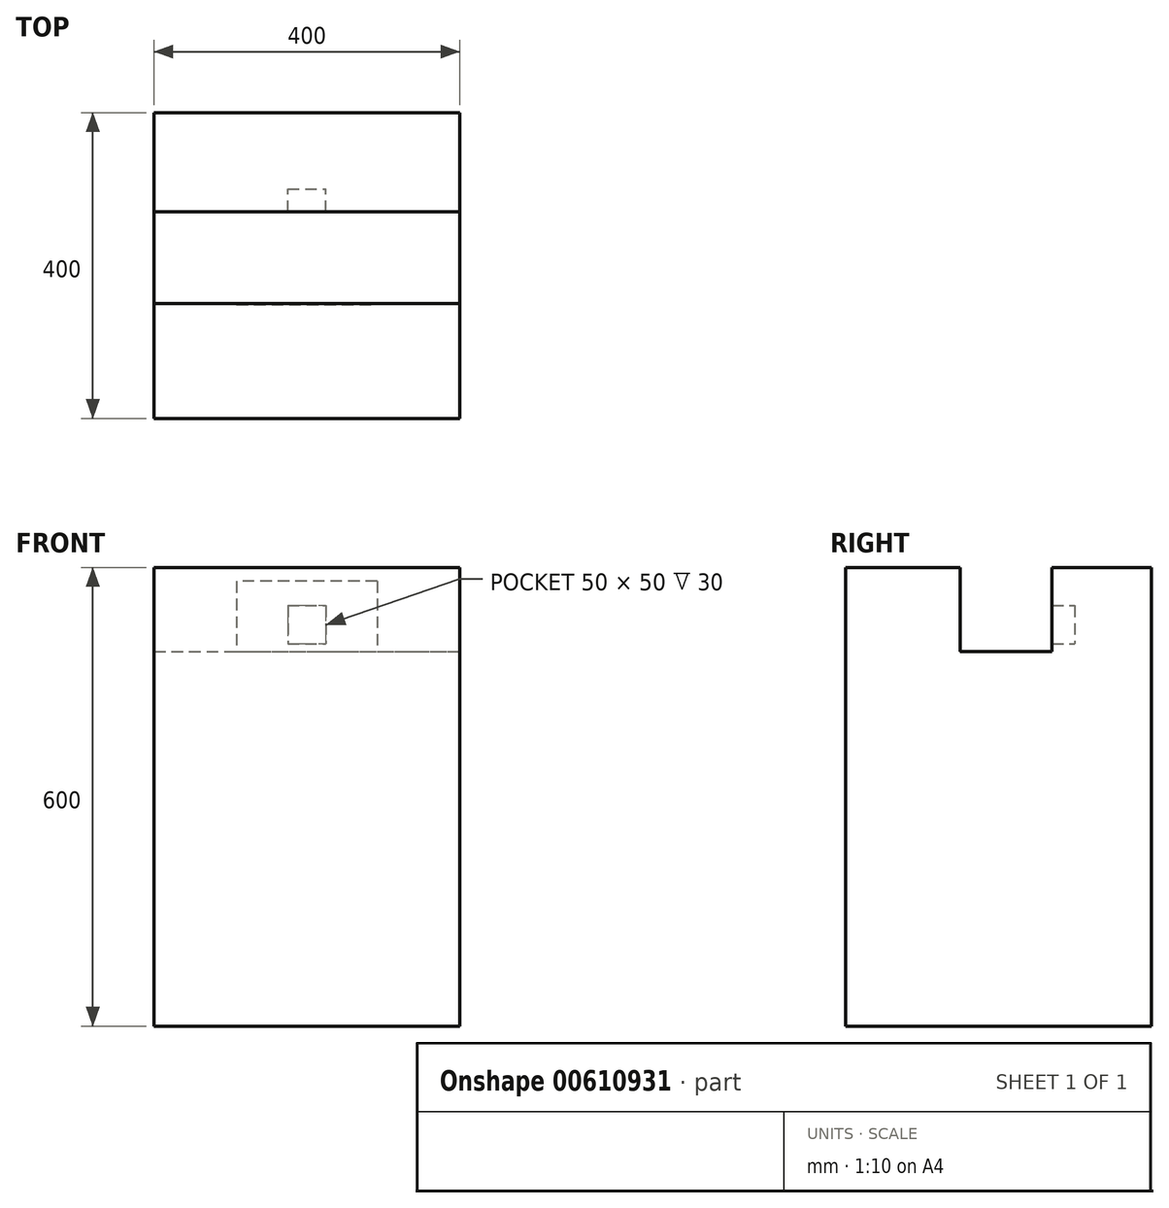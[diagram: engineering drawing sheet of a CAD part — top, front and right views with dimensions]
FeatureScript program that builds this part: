
annotation { "Feature Type Name" : "Feature", "Feature Type Description" : "" }
export const myFeature = defineFeature(function(context is Context, id is Id, definition is map)
    precondition{}
    {
        {
            var Q0;
            Q0=qCreatedBy(makeId("Right.planeOp"),FACE);
            var sketch = newSketch(context, id + "F0", { "sketchPlane" : qUnion([Q0])});
            skLineSegment(sketch, "E0.bottom", {"start": v(0, 0) * mm, "end": v(400, 0) * mm});
            skLineSegment(sketch, "E0.top", {"start": v(0, 600) * mm, "end": v(400, 600) * mm});
            skLineSegment(sketch, "E0.left", {"start": v(0, 0) * mm, "end": v(0, 600) * mm});
            skLineSegment(sketch, "E0.right", {"start": v(400, 0) * mm, "end": v(400, 600) * mm});
            skSolve(sketch);
        }
        {
            var Q0;
            Q0=makeQuery(id+"F0.imprint","IMPRINT",FACE,{"disambiguationData":[TD([[makeQuery(id+"F0.imprint","IMPRINT",EDGE,{"derivedFrom":sQuery(id+"F0.wireOp",EDGE,"E0.bottom")}),1.0]])]});
            extrude(context, id + "F1", {"entities" : qUnion([Q0]), "depth" : 200 * mm, "offsetDistance" : 25 * mm});
        }
        {
            var Q0;
            Q0=makeQuery(id+"F1.opExtrude","CAP_FACE",FACE,{"disambiguationData":[OSD([sQuery(id+"F0.wireOp",EDGE,"E0.bottom"),sQuery(id+"F0.wireOp",EDGE,"E0.top"),sQuery(id+"F0.wireOp",EDGE,"E0.left"),sQuery(id+"F0.wireOp",EDGE,"E0.right")])],"isStart":false});
            var sketch = newSketch(context, id + "F2", { "sketchPlane" : qUnion([Q0])});
            skLineSegment(sketch, "E1.bottom", {"start": v(270, 550) * mm, "end": v(300, 550) * mm});
            skLineSegment(sketch, "E1.top", {"start": v(270, 500) * mm, "end": v(300, 500) * mm});
            skLineSegment(sketch, "E1.left", {"start": v(270, 550) * mm, "end": v(270, 500) * mm});
            skLineSegment(sketch, "E1.right", {"start": v(300, 550) * mm, "end": v(300, 500) * mm});
            skSolve(sketch);
        }
        {
            var Q0;
            Q0=makeQuery(id+"F2.imprint","IMPRINT",FACE,{"disambiguationData":[TD([[makeQuery(id+"F2.imprint","IMPRINT",EDGE,{"derivedFrom":sQuery(id+"F2.wireOp",EDGE,"E1.bottom")}),-1.0]])]});
            extrude(context, id + "F3", {"entities" : qUnion([Q0]), "operationType" : NewBodyOperationType.REMOVE, "oppositeDirection" : true, "depth" : 25 * mm, "offsetDistance" : 25 * mm});
        }
        {
            var Q0;
            Q0=makeQuery(id+"F1.opExtrude","CAP_FACE",FACE,{"disambiguationData":[OSD([sQuery(id+"F0.wireOp",EDGE,"E0.bottom"),sQuery(id+"F0.wireOp",EDGE,"E0.top"),sQuery(id+"F0.wireOp",EDGE,"E0.left"),sQuery(id+"F0.wireOp",EDGE,"E0.right")])],"isStart":false});
            extrude(context, id + "F4", {"entities" : qUnion([Q0]), "operationType" : NewBodyOperationType.ADD, "depth" : 25 * mm, "offsetDistance" : 25 * mm});
        }
        {
            var Q0;
            Q0=makeQuery(id+"F4.opExtrude","CAP_FACE",FACE,{"disambiguationData":[OSD([sQuery(id+"F0.wireOp",EDGE,"E0.bottom"),sQuery(id+"F0.wireOp",EDGE,"E0.top"),sQuery(id+"F0.wireOp",EDGE,"E0.left"),sQuery(id+"F0.wireOp",EDGE,"E0.right")])],"isStart":false});
            var sketch = newSketch(context, id + "F5", { "sketchPlane" : qUnion([Q0])});
            skLineSegment(sketch, "E2.0", {"start": v(0, 600) * mm, "end": v(400, 600) * mm});
            skLineSegment(sketch, "E3.0", {"start": v(0, 0) * mm, "end": v(0, 600) * mm});
            skLineSegment(sketch, "E4.0", {"start": v(0, 0) * mm, "end": v(400, 0) * mm});
            skLineSegment(sketch, "E5.0", {"start": v(400, 0) * mm, "end": v(400, 600) * mm});
            skSolve(sketch);
        }
        {
            var Q0;
            Q0=makeQuery(id+"F5.imprint","IMPRINT",FACE,{"disambiguationData":[TD([[makeQuery(id+"F5.imprint","IMPRINT",EDGE,{"derivedFrom":sQuery(id+"F5.wireOp",EDGE,"E2.0")}),-1.0]])]});
            var Q1;
            Q1=makeQuery(id+"F5.imprint","IMPRINT",FACE,{"disambiguationData":[TD([[makeQuery(id+"F5.imprint","IMPRINT",EDGE,{"derivedFrom":makeQuery(id+"F4.opExtrude","CAP_EDGE",EDGE,{"disambiguationData":[OSD([sQuery(id+"F2.wireOp",EDGE,"E1.bottom")])],"isStart":false})}),-1.0]])]});
            extrude(context, id + "F6", {"entities" : qUnion([Q0, Q1]), "operationType" : NewBodyOperationType.ADD, "depth" : (200 - 25) * mm, "offsetDistance" : 25 * mm});
        }
        {
            var Q0;
            Q0=makeQuery(id+"F6.opExtrude","CAP_FACE",FACE,{"disambiguationData":[OSD([sQuery(id+"F5.wireOp",EDGE,"E2.0"),sQuery(id+"F5.wireOp",EDGE,"E3.0"),sQuery(id+"F5.wireOp",EDGE,"E4.0"),sQuery(id+"F5.wireOp",EDGE,"E5.0")])],"isStart":false});
            var sketch = newSketch(context, id + "F7", { "sketchPlane" : qUnion([Q0])});
            skLineSegment(sketch, "E6.bottom", {"start": v(270, 600) * mm, "end": v(150, 600) * mm});
            skLineSegment(sketch, "E6.top", {"start": v(270, 490) * mm, "end": v(150, 490) * mm});
            skLineSegment(sketch, "E6.left", {"start": v(270, 600) * mm, "end": v(270, 490) * mm});
            skLineSegment(sketch, "E6.right", {"start": v(150, 600) * mm, "end": v(150, 490) * mm});
            skLineSegment(sketch, "E7.0", {"start": v(270, 550) * mm, "end": v(270, 500) * mm});
            skSolve(sketch);
        }
        {
            var Q0;
            {var subQ3=sQuery(id+"F7.wireOp",EDGE,"E6.bottom");Q0=makeQuery(id+"F7.imprint","IMPRINT",FACE,{"disambiguationData":[TD([[makeQuery(id+"F7.imprint","IMPRINT",EDGE,{"derivedFrom":subQ3}),-1.0]])]});}
            extrude(context, id + "F8", {"entities" : qUnion([Q0]), "operationType" : NewBodyOperationType.REMOVE, "endBound" : BoundingType.THROUGH_ALL, "oppositeDirection" : true, "depth" : 25 * mm, "offsetDistance" : 25 * mm});
        }
        {
            var Q0;
            Q0=makeQuery(id+"F8.boolean.opBoolean","COPY",FACE,{"derivedFrom":makeQuery(id+"F8.opExtrude","SWEPT_FACE",FACE,{"disambiguationData":[OSD([sQuery(id+"F7.wireOp",EDGE,"E6.right")])]})});
            var sketch = newSketch(context, id + "F9", { "sketchPlane" : qUnion([Q0])});
            skLineSegment(sketch, "E8.bottom", {"start": v(-292, 582) * mm, "end": v(-108, 582) * mm});
            skLineSegment(sketch, "E8.top", {"start": v(-292, 490) * mm, "end": v(-108, 490) * mm});
            skLineSegment(sketch, "E8.left", {"start": v(-292, 582) * mm, "end": v(-292, 490) * mm});
            skLineSegment(sketch, "E8.right", {"start": v(-108, 582) * mm, "end": v(-108, 490) * mm});
            skSolve(sketch);
        }
        {
            var Q0;
            Q0=makeQuery(id+"F9.imprint","IMPRINT",FACE,{"disambiguationData":[TD([[makeQuery(id+"F9.imprint","IMPRINT",EDGE,{"derivedFrom":sQuery(id+"F9.wireOp",EDGE,"E8.bottom")}),-1.0]])]});
            extrude(context, id + "F10", {"entities" : qUnion([Q0]), "operationType" : NewBodyOperationType.REMOVE, "oppositeDirection" : true, "depth" : 1 * mm, "offsetDistance" : 25 * mm});
        }
    });
